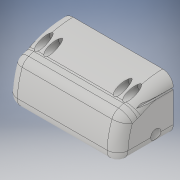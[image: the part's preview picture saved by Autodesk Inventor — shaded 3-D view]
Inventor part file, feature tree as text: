
AUTODESK INVENTOR PART (.ipt)
format: ipt  version: 2017 (Build 210142000, 142)  size: 287,744 bytes
history: native  units: in
note: dims shown in document units (in); Inventor stores cm internally (conversion verified against a paired STEP export)
features: sketch x7, extrude x4, hole x3, fillet x2, plane x1, projected_geometry x1
ambient origin geometry x8: Origin, YZ Plane, XZ Plane, XY Plane, X Axis, Y Axis, Z Axis, Center Point
bodies: Solid1 (feature_tree)
feature tree (18):
  extrude  "Extrusion1"  Depth=1.53in
  fillet  "Fillet5"  Radius=1.6in
  extrude  "Extrusion2"  Depth=1.4in
  fillet  "Fillet6"  Radius=1.1in
  plane  "Work Plane1"
  hole  "Hole1"  [1 undecoded]
  hole  "Hole2"  [1 undecoded]
  hole  "Hole3"  [1 undecoded]
  extrude  "Extrusion3"  Depth=1.6in
  extrude  "Extrusion4"  Depth=0.06in
  sketch  "Sketch1"  dims[d0=3.17in d1=1.53in d2=1.6in d3=0.0in]
  sketch  "Sketch5"  dims[d11=0.3in d12=1.4in d13=1.1in]
  sketch  "Sketch6"  dims[d14=1.25in d15=1.15in]
  sketch  "Sketch7"  dims[d16=0.2in d17=0.3in]
  sketch  "Sketch8"  dims[d18=2.3007in d19=3.7in d20=0.0in]
  sketch  "Sketch9"  dims[d21=0.3in d22=1.6in]
  projected_geometry  "Projected Loop1"
  sketch  "Sketch10"  dims[d23=0.32in d24=0.27in d25=0.18in d26=0.18in d27=0.32in d28=0.27in d29=0.18in d30=0.18in d31=0.2in d32=0.75in d33=0.375in d34=0.25in d35=0.5635in d36=1.0in d37=0.8108in d40=0.3in d41=0.5in d42=0.29in d43=0.75in d44=0.375in d45=0.25in d46=0.5635in d47=0.35in d48=0.8108in d49=0.29in d50=0.75in d51=0.375in d52=0.25in d53=0.5635in d54=0.35in d55=0.8108in d56=0.39in d57=0.39in d58=0.3in d59=0.3in d60=0.2in d61=0.57in d62=0.0in d63=0.3in d64=0.06in d65=0.06in d66=0.3in d67=0.06in d69=0.06in d70=0.57in d71=0.0in]
note: 3 required parameter values undecoded (feature->parameter linkage not recoverable at this tier; creation-order binding heuristic only, values carry confidence <= 0.55)
